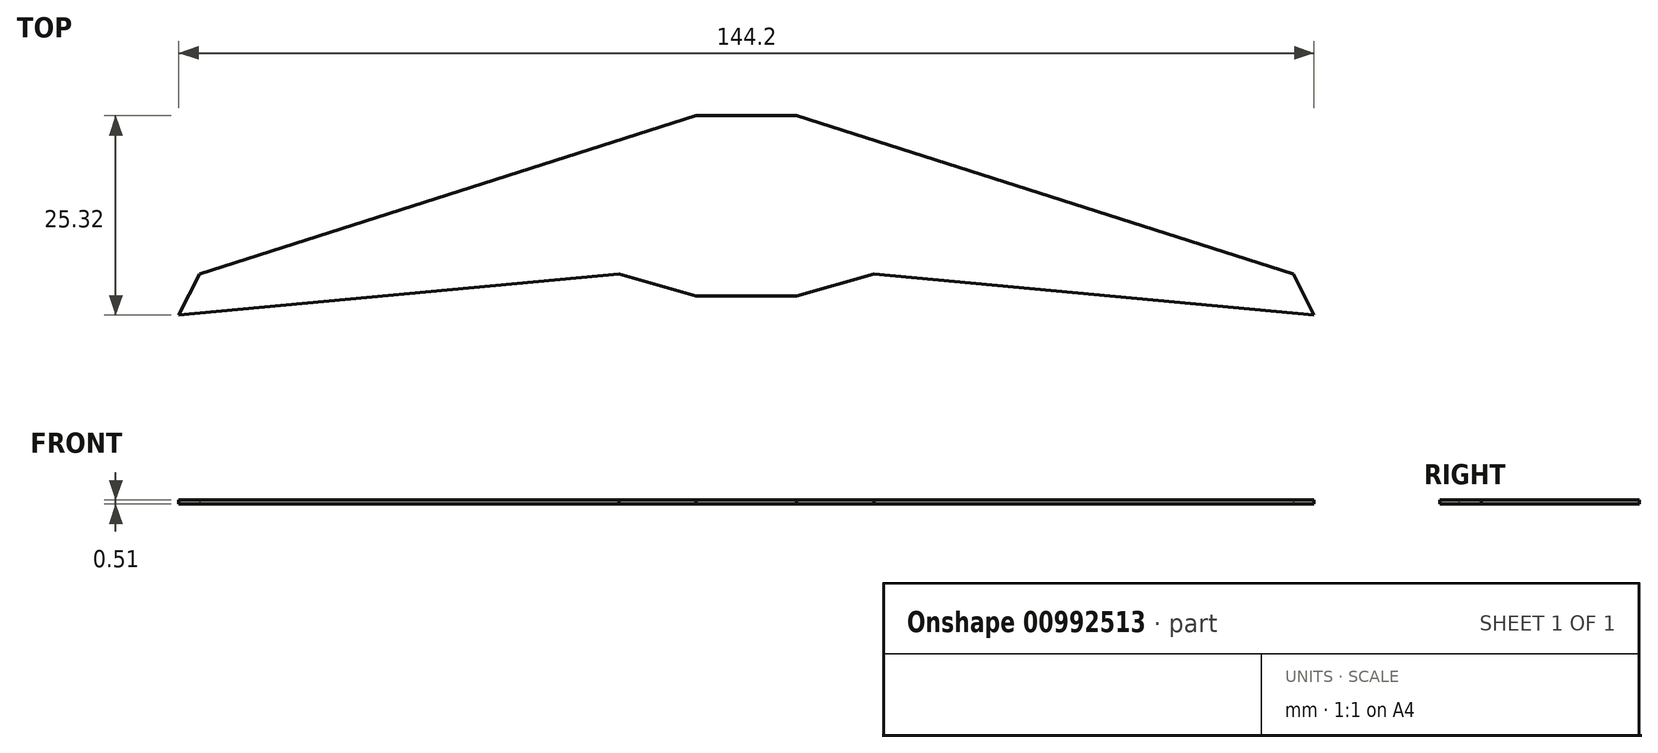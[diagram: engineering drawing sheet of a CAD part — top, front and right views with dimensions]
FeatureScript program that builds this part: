
annotation { "Feature Type Name" : "Feature", "Feature Type Description" : "" }
export const myFeature = defineFeature(function(context is Context, id is Id, definition is map)
    precondition{}
    {
        {
            var Q0;
            Q0=qCreatedBy(makeId("Top.planeOp"),FACE);
            var sketch = newSketch(context, id + "F0", { "sketchPlane" : qUnion([Q0])});
            skLineSegment(sketch, "E0", {"start": v(-5.4, 35.31) * mm, "end": v(6.39, 35.31) * mm});
            skLineSegment(sketch, "E1", {"start": v(6.39, 35.31) * mm, "end": v(69.48, 15.23) * mm});
            skLineSegment(sketch, "E2", {"start": v(69.48, 15.23) * mm, "end": v(72.1, 9.99) * mm});
            skLineSegment(sketch, "E3", {"start": v(72.1, 9.99) * mm, "end": v(16.2, 15.23) * mm});
            skLineSegment(sketch, "E4", {"start": v(16.2, 15.23) * mm, "end": v(6.39, 12.39) * mm});
            skLineSegment(sketch, "E5", {"start": v(0, 35.31) * mm, "end": v(0, 12.39) * mm});
            skPoint(sketch, "E5.startSnap0", {"position": v(0.5, 35.31) * mm});
            skLineSegment(sketch, "E6", {"start": v(6.39, 12.39) * mm, "end": v(0, 12.39) * mm});
            skLineSegment(sketch, "E7.MirrorCS", {"start": v(-6.39, 35.31) * mm, "end": v(-69.48, 15.23) * mm});
            skLineSegment(sketch, "E8.MirrorCS", {"start": v(5.4, 35.31) * mm, "end": v(-6.39, 35.31) * mm});
            skLineSegment(sketch, "E9.MirrorCS", {"start": v(-16.2, 15.23) * mm, "end": v(-6.39, 12.39) * mm});
            skLineSegment(sketch, "E10.MirrorCS", {"start": v(-6.39, 12.39) * mm, "end": v(0, 12.39) * mm});
            skLineSegment(sketch, "E11.MirrorCS", {"start": v(-72.1, 9.99) * mm, "end": v(-16.2, 15.23) * mm});
            skLineSegment(sketch, "E12.MirrorCS", {"start": v(-69.48, 15.23) * mm, "end": v(-72.1, 9.99) * mm});
            skSolve(sketch);
        }
        {
            var Q0;
            {var subQ0=sQuery(id+"F0.wireOp",EDGE,"E0");Q0=makeQuery(id+"F0.imprint","IMPRINT",FACE,{"disambiguationData":[TD([[makeQuery(id+"F0.imprint","IMPRINT",EDGE,{"derivedFrom":subQ0}),-1.0]])]});}
            var Q1;
            {var subQ1=sQuery(id+"F0.wireOp",EDGE,"E5");Q1=makeQuery(id+"F0.imprint","IMPRINT",FACE,{"disambiguationData":[TD([[makeQuery(id+"F0.imprint","IMPRINT",EDGE,{"derivedFrom":subQ1}),-1.0]])]});}
            extrude(context, id + "F1", {"entities" : qUnion([Q0, Q1]), "depth" : 0.5 * mm, "offsetDistance" : 25.4 * mm});
        }
    });
